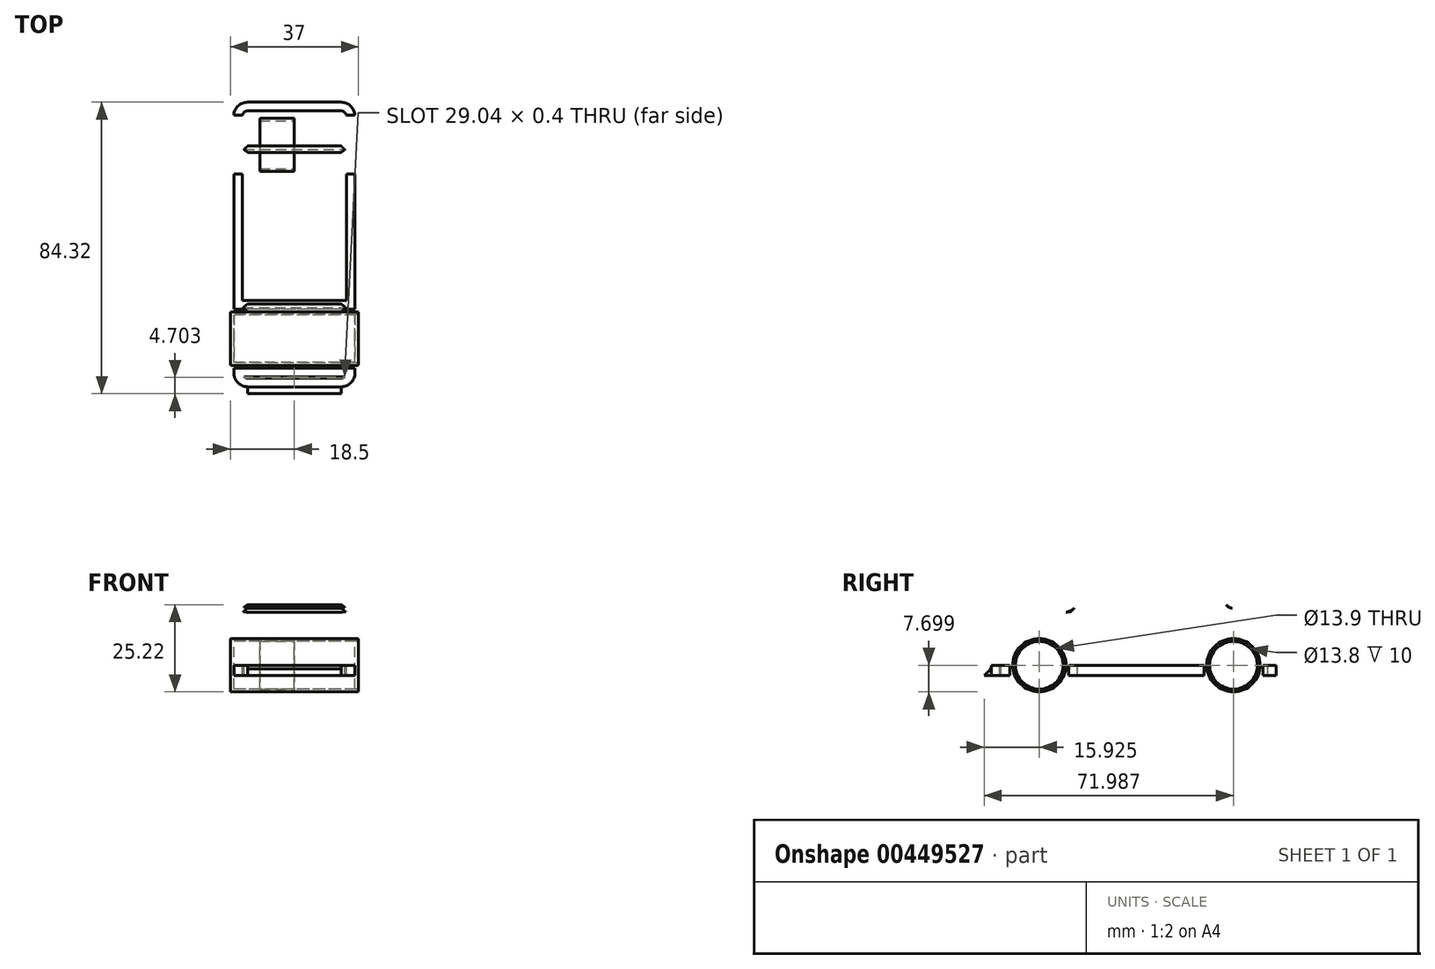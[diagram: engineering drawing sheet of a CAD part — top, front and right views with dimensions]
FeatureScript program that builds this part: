
annotation { "Feature Type Name" : "Feature", "Feature Type Description" : "" }
export const myFeature = defineFeature(function(context is Context, id is Id, definition is map)
    precondition{}
    {
        {
            var Q0;
            Q0=qCreatedBy(makeId("Right.planeOp"),FACE);
            var sketch = newSketch(context, id + "F0", { "sketchPlane" : qUnion([Q0])});
            skLineSegment(sketch, "E0", {"start": v(-46.86, -9.62) * mm, "end": v(35.46, -9.62) * mm});
            skLineSegment(sketch, "E1", {"start": v(35.46, -9.62) * mm, "end": v(35.46, 3.56) * mm});
            skLineSegment(sketch, "E2", {"start": v(35.46, 3.56) * mm, "end": v(21.74, 7.13) * mm});
            skLineSegment(sketch, "E3", {"start": v(21.74, 7.13) * mm, "end": v(13.72, 15.14) * mm});
            skLineSegment(sketch, "E4", {"start": v(13.72, 15.14) * mm, "end": v(-14.43, 15.14) * mm});
            skLineSegment(sketch, "E5", {"start": v(-14.43, 15.14) * mm, "end": v(-23.87, 5.88) * mm});
            skLineSegment(sketch, "E6", {"start": v(-23.87, 5.88) * mm, "end": v(-46.5, 3.03) * mm});
            skLineSegment(sketch, "E7", {"start": v(-46.5, 3.03) * mm, "end": v(-46.86, -9.62) * mm});
            skCircle(sketch, "E8", {"center": v(-32.94, -9.62) * mm, "radius": 8.52 * mm});
            skCircle(sketch, "E9", {"center": v(23.13, -9.62) * mm, "radius": 8.54 * mm});
            skSolve(sketch);
        }
        {
            var Q0;
            {var subQ4=sQuery(id+"F0.wireOp",EDGE,"E1");Q0=makeQuery(id+"F0.imprint","IMPRINT",FACE,{"disambiguationData":[TD([[makeQuery(id+"F0.imprint","IMPRINT",EDGE,{"derivedFrom":subQ4}),1.0]])]});}
            var Q1;
            {var subQ0=sQuery(id+"F0.wireOp",EDGE,"E8");var subQ1=sQuery(id+"F0.wireOp",EDGE,"E0");var subQ2=makeQuery(id+"F0.imprint","INTERSECT",VERTEX,{"disambiguationData":[OD(0.0)],"derivedFrom":[subQ1,subQ0]});Q1=makeQuery(id+"F0.imprint","IMPRINT",FACE,{"disambiguationData":[TD([[makeQuery(id+"F0.imprint","IMPRINT",EDGE,{"disambiguationData":[TD([[subQ2,-1.0]])],"derivedFrom":subQ1}),1.0]])]});}
            var Q2;
            {var subQ0=sQuery(id+"F0.wireOp",EDGE,"E9");var subQ1=sQuery(id+"F0.wireOp",EDGE,"E0");var subQ2=makeQuery(id+"F0.imprint","INTERSECT",VERTEX,{"disambiguationData":[OD(0.0)],"derivedFrom":[subQ1,subQ0]});Q2=makeQuery(id+"F0.imprint","IMPRINT",FACE,{"disambiguationData":[TD([[makeQuery(id+"F0.imprint","IMPRINT",EDGE,{"disambiguationData":[TD([[subQ2,-1.0]])],"derivedFrom":subQ1}),1.0]])]});}
            extrude(context, id + "F1", {"entities" : qUnion([Q0, Q1, Q2]), "endBound" : BoundingType.SYMMETRIC, "depth" : 35 * mm});
        }
        {
            var Q0;
            Q0=makeQuery(id+"F1.opExtrude","CAP_EDGE",EDGE,{"disambiguationData":[OSD([sQuery(id+"F0.wireOp",EDGE,"E7")])],"isStart":false});
            var Q1;
            Q1=makeQuery(id+"F1.opExtrude","CAP_EDGE",EDGE,{"disambiguationData":[OSD([sQuery(id+"F0.wireOp",EDGE,"E6")])],"isStart":false});
            var Q2;
            Q2=makeQuery(id+"F1.opExtrude","SWEPT_EDGE",EDGE,{"disambiguationData":[OSD([sQuery(id+"F0.wireOp",EDGE,"E6"),sQuery(id+"F0.wireOp",EDGE,"E7")])]});
            var Q3;
            Q3=makeQuery(id+"F1.opExtrude","CAP_EDGE",EDGE,{"disambiguationData":[OSD([sQuery(id+"F0.wireOp",EDGE,"E5")])],"isStart":false});
            var Q4;
            Q4=makeQuery(id+"F1.opExtrude","SWEPT_EDGE",EDGE,{"disambiguationData":[OSD([sQuery(id+"F0.wireOp",EDGE,"E4"),sQuery(id+"F0.wireOp",EDGE,"E5")])]});
            var Q5;
            Q5=makeQuery(id+"F1.opExtrude","SWEPT_EDGE",EDGE,{"disambiguationData":[OSD([sQuery(id+"F0.wireOp",EDGE,"E5"),sQuery(id+"F0.wireOp",EDGE,"E6")])]});
            var Q6;
            Q6=makeQuery(id+"F1.opExtrude","CAP_EDGE",EDGE,{"disambiguationData":[OSD([sQuery(id+"F0.wireOp",EDGE,"E4")])],"isStart":false});
            var Q7;
            Q7=makeQuery(id+"F1.opExtrude","SWEPT_EDGE",EDGE,{"disambiguationData":[OSD([sQuery(id+"F0.wireOp",EDGE,"E3"),sQuery(id+"F0.wireOp",EDGE,"E4")])]});
            var Q8;
            Q8=makeQuery(id+"F1.opExtrude","SWEPT_EDGE",EDGE,{"disambiguationData":[OSD([sQuery(id+"F0.wireOp",EDGE,"E2"),sQuery(id+"F0.wireOp",EDGE,"E3")])]});
            var Q9;
            Q9=makeQuery(id+"F1.opExtrude","CAP_EDGE",EDGE,{"disambiguationData":[OSD([sQuery(id+"F0.wireOp",EDGE,"E2")])],"isStart":false});
            var Q10;
            Q10=makeQuery(id+"F1.opExtrude","SWEPT_EDGE",EDGE,{"disambiguationData":[OSD([sQuery(id+"F0.wireOp",EDGE,"E1"),sQuery(id+"F0.wireOp",EDGE,"E2")])]});
            var Q11;
            Q11=makeQuery(id+"F1.opExtrude","CAP_EDGE",EDGE,{"disambiguationData":[OSD([sQuery(id+"F0.wireOp",EDGE,"E2")])],"isStart":true});
            var Q12;
            Q12=makeQuery(id+"F1.opExtrude","CAP_EDGE",EDGE,{"disambiguationData":[OSD([sQuery(id+"F0.wireOp",EDGE,"E1")])],"isStart":true});
            var Q13;
            Q13=makeQuery(id+"F1.opExtrude","CAP_EDGE",EDGE,{"disambiguationData":[OSD([sQuery(id+"F0.wireOp",EDGE,"E4")])],"isStart":true});
            var Q14;
            Q14=makeQuery(id+"F1.opExtrude","CAP_EDGE",EDGE,{"disambiguationData":[OSD([sQuery(id+"F0.wireOp",EDGE,"E5")])],"isStart":true});
            var Q15;
            Q15=makeQuery(id+"F1.opExtrude","CAP_EDGE",EDGE,{"disambiguationData":[OSD([sQuery(id+"F0.wireOp",EDGE,"E6")])],"isStart":true});
            var Q16;
            Q16=makeQuery(id+"F1.opExtrude","CAP_EDGE",EDGE,{"disambiguationData":[OSD([sQuery(id+"F0.wireOp",EDGE,"E7")])],"isStart":true});
            var Q17;
            Q17=makeQuery(id+"F1.opExtrude","CAP_EDGE",EDGE,{"disambiguationData":[OSD([sQuery(id+"F0.wireOp",EDGE,"E3")])],"isStart":false});
            var Q18;
            Q18=makeQuery(id+"F1.opExtrude","CAP_EDGE",EDGE,{"disambiguationData":[OSD([sQuery(id+"F0.wireOp",EDGE,"E3")])],"isStart":true});
            var Q19;
            Q19=makeQuery(id+"F1.opExtrude","CAP_EDGE",EDGE,{"disambiguationData":[OSD([sQuery(id+"F0.wireOp",EDGE,"E1")])],"isStart":false});
            fillet(context, id + "F2", {"entities" : qUnion([Q0, Q1, Q2, Q3, Q4, Q5, Q6, Q7, Q8, Q9, Q10, Q11, Q12, Q13, Q14, Q15, Q16, Q17, Q18, Q19]), "radius" : 4 * mm, "tangentPropagation" : true, "allowEdgeOverflow" : false});
        }
        {
            var Q0;
            Q0=makeQuery(id+"F1.opExtrude","SWEPT_FACE",FACE,{"disambiguationData":[OSD([sQuery(id+"F0.wireOp",EDGE,"E0")])]});
            shell(context, id + "F3", {"entities" : qUnion([Q0]), "thickness" : 2.5 * mm});
        }
        {
            var Q0;
            {var subQ0=sQuery(id+"F0.wireOp",EDGE,"E7");var subQ1=sQuery(id+"F0.wireOp",EDGE,"E6");var subQ2=sQuery(id+"F0.wireOp",EDGE,"E5");var subQ3=sQuery(id+"F0.wireOp",EDGE,"E4");var subQ4=sQuery(id+"F0.wireOp",EDGE,"E3");var subQ5=sQuery(id+"F0.wireOp",EDGE,"E2");var subQ6=sQuery(id+"F0.wireOp",EDGE,"E1");var subQ7=sQuery(id+"F0.wireOp",EDGE,"E0");var subQ8=makeQuery(id+"F1.opExtrude","CAP_FACE",FACE,{"disambiguationData":[OSD([subQ7,subQ6,subQ5,subQ4,subQ3,subQ2,subQ1,subQ0])],"isStart":true});Q0=makeQuery(id+"FvR2XKBQ7TzLp4t_1.boolean.opBoolean","SPLIT",FACE,{"disambiguationData":[TD([subQ8,makeQuery(id+"F3.opShell","OFFSET_FACE",FACE,{"disambiguationData":[OSD([subQ7,subQ6,subQ5,subQ4,subQ3,subQ2,subQ1,subQ0]),TDD([subQ8])]}),makeQuery(id+"FvR2XKBQ7TzLp4t_1.opExtrude","SWEPT_FACE",FACE,{"disambiguationData":[OSD([sQuery(id+"F0.wireOp",EDGE,"E8")])]}),makeQuery(id+"FvR2XKBQ7TzLp4t_1.opExtrude","SWEPT_FACE",FACE,{"disambiguationData":[OSD([sQuery(id+"F0.wireOp",EDGE,"E9")])]})])],"derivedFrom":makeQuery(id+"F1.opExtrude","SWEPT_FACE",FACE,{"disambiguationData":[OSD([subQ7])]})});}
            var Q1;
            {var subQ0=sQuery(id+"F0.wireOp",EDGE,"E7");var subQ1=makeQuery(id+"F1.opExtrude","SWEPT_FACE",FACE,{"disambiguationData":[OSD([subQ0])]});var subQ2=sQuery(id+"F0.wireOp",EDGE,"E6");var subQ3=sQuery(id+"F0.wireOp",EDGE,"E5");var subQ4=sQuery(id+"F0.wireOp",EDGE,"E4");var subQ5=sQuery(id+"F0.wireOp",EDGE,"E3");var subQ6=sQuery(id+"F0.wireOp",EDGE,"E2");var subQ7=sQuery(id+"F0.wireOp",EDGE,"E1");var subQ8=sQuery(id+"F0.wireOp",EDGE,"E0");var subQ9=makeQuery(id+"F1.opExtrude","CAP_FACE",FACE,{"disambiguationData":[OSD([subQ8,subQ7,subQ6,subQ5,subQ4,subQ3,subQ2,subQ0])],"isStart":false});var subQ10=makeQuery(id+"F1.opExtrude","CAP_FACE",FACE,{"disambiguationData":[OSD([subQ8,subQ7,subQ6,subQ5,subQ4,subQ3,subQ2,subQ0])],"isStart":true});var subQ11=makeQuery(id+"F2.opFillet","BLEND_FACE",FACE,{"disambiguationData":[OSD([subQ0]),TDD([makeQuery(id+"F1.opExtrude","CAP_EDGE",EDGE,{"disambiguationData":[OSD([subQ0])],"isStart":false})])]});var subQ12=makeQuery(id+"F2.opFillet","BLEND_FACE",FACE,{"disambiguationData":[OSD([subQ0]),TDD([makeQuery(id+"F1.opExtrude","CAP_EDGE",EDGE,{"disambiguationData":[OSD([subQ0])],"isStart":true})])]});Q1=makeQuery(id+"FvR2XKBQ7TzLp4t_1.boolean.opBoolean","SPLIT",FACE,{"disambiguationData":[TD([subQ10,subQ9,subQ1,subQ12,subQ11,makeQuery(id+"F3.opShell","OFFSET_FACE",FACE,{"disambiguationData":[OSD([subQ0]),TDD([subQ12])]}),makeQuery(id+"F3.opShell","OFFSET_FACE",FACE,{"disambiguationData":[OSD([subQ0]),TDD([subQ11])]}),makeQuery(id+"F3.opShell","OFFSET_FACE",FACE,{"disambiguationData":[OSD([subQ8,subQ7,subQ6,subQ5,subQ4,subQ3,subQ2,subQ0]),TDD([subQ10])]}),makeQuery(id+"F3.opShell","OFFSET_FACE",FACE,{"disambiguationData":[OSD([subQ8,subQ7,subQ6,subQ5,subQ4,subQ3,subQ2,subQ0]),TDD([subQ9])]}),makeQuery(id+"F3.opShell","OFFSET_FACE",FACE,{"disambiguationData":[OSD([subQ0]),TDD([subQ1])]}),makeQuery(id+"FvR2XKBQ7TzLp4t_1.opExtrude","SWEPT_FACE",FACE,{"disambiguationData":[OSD([sQuery(id+"F0.wireOp",EDGE,"E8")])]})])],"derivedFrom":makeQuery(id+"F1.opExtrude","SWEPT_FACE",FACE,{"disambiguationData":[OSD([subQ8])]})});}
            var Q2;
            {var subQ0=sQuery(id+"F0.wireOp",EDGE,"E7");var subQ1=sQuery(id+"F0.wireOp",EDGE,"E6");var subQ2=sQuery(id+"F0.wireOp",EDGE,"E5");var subQ3=sQuery(id+"F0.wireOp",EDGE,"E4");var subQ4=sQuery(id+"F0.wireOp",EDGE,"E3");var subQ5=sQuery(id+"F0.wireOp",EDGE,"E2");var subQ6=sQuery(id+"F0.wireOp",EDGE,"E1");var subQ7=sQuery(id+"F0.wireOp",EDGE,"E0");var subQ8=makeQuery(id+"F1.opExtrude","CAP_FACE",FACE,{"disambiguationData":[OSD([subQ7,subQ6,subQ5,subQ4,subQ3,subQ2,subQ1,subQ0])],"isStart":false});Q2=makeQuery(id+"FvR2XKBQ7TzLp4t_1.boolean.opBoolean","SPLIT",FACE,{"disambiguationData":[TD([subQ8,makeQuery(id+"F3.opShell","OFFSET_FACE",FACE,{"disambiguationData":[OSD([subQ7,subQ6,subQ5,subQ4,subQ3,subQ2,subQ1,subQ0]),TDD([subQ8])]}),makeQuery(id+"FvR2XKBQ7TzLp4t_1.opExtrude","SWEPT_FACE",FACE,{"disambiguationData":[OSD([sQuery(id+"F0.wireOp",EDGE,"E8")])]}),makeQuery(id+"FvR2XKBQ7TzLp4t_1.opExtrude","SWEPT_FACE",FACE,{"disambiguationData":[OSD([sQuery(id+"F0.wireOp",EDGE,"E9")])]})])],"derivedFrom":makeQuery(id+"F1.opExtrude","SWEPT_FACE",FACE,{"disambiguationData":[OSD([subQ7])]})});}
            var Q3;
            {var subQ0=sQuery(id+"F0.wireOp",EDGE,"E1");var subQ1=makeQuery(id+"F2.opFillet","BLEND_FACE",FACE,{"disambiguationData":[OSD([subQ0]),TDD([makeQuery(id+"F1.opExtrude","CAP_EDGE",EDGE,{"disambiguationData":[OSD([subQ0])],"isStart":true})])]});var subQ2=makeQuery(id+"F2.opFillet","BLEND_FACE",FACE,{"disambiguationData":[OSD([subQ0]),TDD([makeQuery(id+"F1.opExtrude","CAP_EDGE",EDGE,{"disambiguationData":[OSD([subQ0])],"isStart":false})])]});var subQ3=makeQuery(id+"F1.opExtrude","SWEPT_FACE",FACE,{"disambiguationData":[OSD([subQ0])]});Q3=makeQuery(id+"FvR2XKBQ7TzLp4t_1.boolean.opBoolean","SPLIT",FACE,{"disambiguationData":[TD([subQ3,subQ1,subQ2,makeQuery(id+"F3.opShell","OFFSET_FACE",FACE,{"disambiguationData":[OSD([subQ0]),TDD([subQ1])]}),makeQuery(id+"F3.opShell","OFFSET_FACE",FACE,{"disambiguationData":[OSD([subQ0]),TDD([subQ2])]}),makeQuery(id+"F3.opShell","OFFSET_FACE",FACE,{"disambiguationData":[OSD([subQ0]),TDD([subQ3])]}),makeQuery(id+"FvR2XKBQ7TzLp4t_1.opExtrude","SWEPT_FACE",FACE,{"disambiguationData":[OSD([sQuery(id+"F0.wireOp",EDGE,"E9")])]})])],"derivedFrom":makeQuery(id+"F1.opExtrude","SWEPT_FACE",FACE,{"disambiguationData":[OSD([sQuery(id+"F0.wireOp",EDGE,"E0")])]})});}
            extrude(context, id + "F4", {"entities" : qUnion([Q0, Q1, Q2, Q3]), "operationType" : NewBodyOperationType.ADD, "depth" : 3 * mm});
        }
        {
            var Q0;
            {var subQ0=sQuery(id+"F0.wireOp",EDGE,"E7");var subQ1=sQuery(id+"F0.wireOp",EDGE,"E0");Q0=makeQuery(id+"F4.opExtrude","SWEPT_FACE",FACE,{"disambiguationData":[OSD([subQ1,subQ0]),TDD([makeQuery(id+"F1.opExtrude","SWEPT_EDGE",EDGE,{"disambiguationData":[OSD([subQ1,subQ0])]})])]});}
            extrude(context, id + "F5", {"entities" : qUnion([Q0]), "operationType" : NewBodyOperationType.ADD, "depth" : 2 * mm});
        }
        {
            var Q0;
            {var subQ0=sQuery(id+"F0.wireOp",EDGE,"E7");var subQ1=sQuery(id+"F0.wireOp",EDGE,"E0");var subQ2=makeQuery(id+"F1.opExtrude","SWEPT_EDGE",EDGE,{"disambiguationData":[OSD([subQ1,subQ0])]});Q0=makeQuery(id+"F5.opExtrude","CAP_EDGE",EDGE,{"disambiguationData":[OSD([subQ1,subQ0]),TDD([makeQuery(id+"F4.boolean.opBoolean","MERGE",EDGE,{"derivedFrom":[subQ2,makeQuery(id+"F4.opExtrude","CAP_EDGE",EDGE,{"disambiguationData":[OSD([subQ1,subQ0]),TDD([subQ2])],"isStart":true})]})])],"isStart":false});}
            chamfer(context, id + "F6", {"entities" : qUnion([Q0]), "width" : 3 * mm, "tangentPropagation" : true});
        }
        {
            var Q0;
            Q0=makeQuery(id+"F1.opExtrude","SWEPT_FACE",FACE,{"disambiguationData":[OSD([sQuery(id+"F0.wireOp",EDGE,"E5")])]});
            extrude(context, id + "F7", {"entities" : qUnion([Q0]), "operationType" : NewBodyOperationType.REMOVE, "oppositeDirection" : true, "depth" : 2.5 * mm});
        }
        {
            var Q0;
            {var subQ0=sQuery(id+"F0.wireOp",EDGE,"E5");var subQ1=makeQuery(id+"F2.opFillet","BLEND_EDGE",EDGE,{"blendedFrom":[makeQuery(id+"F1.opExtrude","CAP_EDGE",EDGE,{"disambiguationData":[OSD([subQ0])],"isStart":true}),makeQuery(id+"F1.opExtrude","SWEPT_FACE",FACE,{"disambiguationData":[OSD([subQ0])]})],"blendedInto":[makeQuery(id+"F1.opExtrude","SWEPT_FACE",FACE,{"disambiguationData":[OSD([subQ0])]})]});Q0=makeQuery(id+"F7.boolean.opBoolean","MERGE",EDGE,{"derivedFrom":[makeQuery(id+"F3.opShell","OFFSET_EDGE",EDGE,{"disambiguationData":[OSD([subQ0]),TDD([subQ1])]}),makeQuery(id+"F7.opExtrude","CAP_EDGE",EDGE,{"disambiguationData":[OSD([subQ0]),TDD([subQ1])],"isStart":false})]});}
            chamfer(context, id + "F8", {"entities" : qUnion([Q0]), "width" : 5 * mm, "tangentPropagation" : true});
        }
        {
            var Q0;
            Q0=qCreatedBy(makeId("Right.planeOp"),FACE);
            var sketch = newSketch(context, id + "F9", { "sketchPlane" : qUnion([Q0])});
            skLineSegment(sketch, "E10", {"start": v(-12.8, 11.13) * mm, "end": v(-21.96, 2.12) * mm});
            skLineSegment(sketch, "E11", {"start": v(-21.96, 2.12) * mm, "end": v(-1.75, 2.12) * mm});
            skLineSegment(sketch, "E12", {"start": v(-1.75, 2.12) * mm, "end": v(-1.75, 11.1) * mm});
            skLineSegment(sketch, "E13", {"start": v(-1.75, 11.1) * mm, "end": v(-12.8, 11.13) * mm});
            skLineSegment(sketch, "E14", {"start": v(1.62, 2.12) * mm, "end": v(1.62, 11.03) * mm});
            skLineSegment(sketch, "E15", {"start": v(1.62, 11.03) * mm, "end": v(12.11, 11.03) * mm});
            skLineSegment(sketch, "E16", {"start": v(12.11, 11.03) * mm, "end": v(20.89, 2.12) * mm});
            skLineSegment(sketch, "E17", {"start": v(20.89, 2.12) * mm, "end": v(1.62, 2.12) * mm});
            skSolve(sketch);
        }
        {
            var Q0;
            Q0 = qSketchRegion(id + "F9", true);
            extrude(context, id + "F10", {"entities" : qUnion([Q0]), "operationType" : NewBodyOperationType.REMOVE, "endBound" : BoundingType.SYMMETRIC, "oppositeDirection" : true, "depth" : 35 * mm});
        }
        {
            var Q0;
            {var subQ0=sQuery(id+"F0.wireOp",EDGE,"E8");var subQ1=sQuery(id+"F0.wireOp",EDGE,"E0");var subQ2=makeQuery(id+"F0.imprint","INTERSECT",VERTEX,{"disambiguationData":[OD(0.0)],"derivedFrom":[subQ1,subQ0]});Q0=makeQuery(id+"F0.imprint","IMPRINT",FACE,{"disambiguationData":[TD([[makeQuery(id+"F0.imprint","IMPRINT",EDGE,{"disambiguationData":[TD([[subQ2,-1.0]])],"derivedFrom":subQ1}),1.0]])]});}
            var Q1;
            {var subQ0=sQuery(id+"F0.wireOp",EDGE,"E9");var subQ1=sQuery(id+"F0.wireOp",EDGE,"E0");var subQ2=makeQuery(id+"F0.imprint","INTERSECT",VERTEX,{"disambiguationData":[OD(0.0)],"derivedFrom":[subQ1,subQ0]});Q1=makeQuery(id+"F0.imprint","IMPRINT",FACE,{"disambiguationData":[TD([[makeQuery(id+"F0.imprint","IMPRINT",EDGE,{"disambiguationData":[TD([[subQ2,-1.0]])],"derivedFrom":subQ1}),1.0]])]});}
            extrude(context, id + "F11", {"entities" : qUnion([Q0, Q1]), "operationType" : NewBodyOperationType.REMOVE, "endBound" : BoundingType.SYMMETRIC, "oppositeDirection" : true, "depth" : 35 * mm});
        }
        {
            var Q0;
            Q0=qCreatedBy(makeId("Right.planeOp"),FACE);
            var sketch = newSketch(context, id + "F12", { "sketchPlane" : qUnion([Q0])});
            skLineSegment(sketch, "E18", {"start": v(-41.46, -9.6) * mm, "end": v(-41.46, -13.06) * mm});
            skLineSegment(sketch, "E19", {"start": v(-24.44, -9.5) * mm, "end": v(-24.44, -13.08) * mm});
            skLineSegment(sketch, "E20", {"start": v(-24.44, -13.08) * mm, "end": v(-41.46, -13.06) * mm});
            skLineSegment(sketch, "E21", {"start": v(-41.46, -9.6) * mm, "end": v(-24.44, -9.5) * mm});
            skSolve(sketch);
        }
        {
            var Q0;
            Q0 = qSketchRegion(id + "F12", true);
            extrude(context, id + "F13", {"entities" : qUnion([Q0]), "operationType" : NewBodyOperationType.REMOVE, "endBound" : BoundingType.SYMMETRIC, "oppositeDirection" : true, "depth" : 35 * mm});
        }
        {
            var Q0;
            Q0=qCreatedBy(makeId("Right.planeOp"),FACE);
            var sketch = newSketch(context, id + "F14", { "sketchPlane" : qUnion([Q0])});
            skLineSegment(sketch, "E22", {"start": v(14.62, -9.53) * mm, "end": v(14.62, -13.62) * mm});
            skLineSegment(sketch, "E23", {"start": v(31.64, -9.47) * mm, "end": v(31.64, -13.06) * mm});
            skLineSegment(sketch, "E24", {"start": v(31.64, -13.06) * mm, "end": v(14.62, -13.62) * mm});
            skLineSegment(sketch, "E25", {"start": v(14.62, -9.53) * mm, "end": v(31.64, -9.47) * mm});
            skSolve(sketch);
        }
        {
            var Q0;
            Q0 = qSketchRegion(id + "F14", true);
            extrude(context, id + "F15", {"entities" : qUnion([Q0]), "operationType" : NewBodyOperationType.REMOVE, "endBound" : BoundingType.SYMMETRIC, "oppositeDirection" : true, "depth" : 35 * mm});
        }
        {
            var Q0;
            Q0 = qSketchRegion(id + "F9", true);
            extrude(context, id + "F16", {"entities" : qUnion([Q0]), "operationType" : NewBodyOperationType.REMOVE, "oppositeDirection" : true, "depth" : 35 * mm});
        }
        {
            var Q0;
            {var subQ0=sQuery(id+"F0.wireOp",EDGE,"E8");var subQ1=sQuery(id+"F0.wireOp",EDGE,"E0");var subQ2=makeQuery(id+"F0.imprint","INTERSECT",VERTEX,{"disambiguationData":[OD(0.0)],"derivedFrom":[subQ1,subQ0]});Q0=makeQuery(id+"F0.imprint","IMPRINT",FACE,{"disambiguationData":[TD([[makeQuery(id+"F0.imprint","IMPRINT",EDGE,{"disambiguationData":[TD([[subQ2,-1.0]])],"derivedFrom":subQ1}),1.0]])]});}
            var sketch = newSketch(context, id + "F17", { "sketchPlane" : qUnion([Q0])});
            skCircle(sketch, "E26", {"center": v(-32.94, -9.62) * mm, "radius": 7.7 * mm});
            skCircle(sketch, "E27", {"center": v(-32.94, -9.62) * mm, "radius": 6.9 * mm});
            skCircle(sketch, "E28", {"center": v(23.13, -9.62) * mm, "radius": 7.7 * mm});
            skCircle(sketch, "E29", {"center": v(23.13, -9.62) * mm, "radius": 6.9 * mm});
            skCircle(sketch, "E30", {"center": v(-32.94, -9.62) * mm, "radius": 6.95 * mm});
            skSolve(sketch);
        }
        {
            var Q0;
            {var subQ0=sQuery(id+"F17.wireOp",EDGE,"E26");var subQ1=sQuery(id+"F0.wireOp",EDGE,"E8");var subQ2=sQuery(id+"F0.wireOp",EDGE,"E0");var subQ3=makeQuery(id+"F0.imprint","IMPRINT",EDGE,{"disambiguationData":[TD([[makeQuery(id+"F0.imprint","INTERSECT",VERTEX,{"disambiguationData":[OD(0.0)],"derivedFrom":[subQ2,subQ1]}),-1.0]])],"derivedFrom":subQ2});var subQ4=makeQuery(id+"F17.imprint","INTERSECT",VERTEX,{"disambiguationData":[OD(0.0)],"derivedFrom":[subQ3,subQ0]});Q0=makeQuery(id+"F17.imprint","IMPRINT",FACE,{"disambiguationData":[TD([[makeQuery(id+"F17.imprint","IMPRINT",EDGE,{"disambiguationData":[TD([[subQ4,-1.0]])],"derivedFrom":subQ0}),1.0]])]});}
            var Q1;
            {var subQ0=sQuery(id+"F17.wireOp",EDGE,"E26");var subQ1=sQuery(id+"F0.wireOp",EDGE,"E8");var subQ2=sQuery(id+"F0.wireOp",EDGE,"E0");var subQ3=makeQuery(id+"F0.imprint","IMPRINT",EDGE,{"disambiguationData":[TD([[makeQuery(id+"F0.imprint","INTERSECT",VERTEX,{"disambiguationData":[OD(0.0)],"derivedFrom":[subQ2,subQ1]}),-1.0]])],"derivedFrom":subQ2});var subQ4=makeQuery(id+"F17.imprint","INTERSECT",VERTEX,{"disambiguationData":[OD(0.0)],"derivedFrom":[subQ3,subQ0]});Q1=makeQuery(id+"F17.imprint","IMPRINT",FACE,{"disambiguationData":[TD([[makeQuery(id+"F17.imprint","IMPRINT",EDGE,{"disambiguationData":[TD([[subQ4,1.0]])],"derivedFrom":subQ0}),1.0]])]});}
            var Q2;
            Q2=sQuery(id+"F17.wireOp",EDGE,"E26");
            var Q3;
            Q3=sQuery(id+"F17.wireOp",EDGE,"E27");
            extrude(context, id + "F18", {"entities" : qUnion([Q0, Q1]), "surfaceEntities" : qUnion([Q2, Q3]), "endBound" : BoundingType.SYMMETRIC, "depth" : 37 * mm});
        }
        {
            var Q0;
            {var subQ0=sQuery(id+"F17.wireOp",EDGE,"E27");var subQ1=sQuery(id+"F0.wireOp",EDGE,"E8");var subQ2=sQuery(id+"F0.wireOp",EDGE,"E0");var subQ3=makeQuery(id+"F0.imprint","IMPRINT",EDGE,{"disambiguationData":[TD([[makeQuery(id+"F0.imprint","INTERSECT",VERTEX,{"disambiguationData":[OD(0.0)],"derivedFrom":[subQ2,subQ1]}),-1.0]])],"derivedFrom":subQ2});var subQ4=makeQuery(id+"F17.imprint","INTERSECT",VERTEX,{"disambiguationData":[OD(0.0)],"derivedFrom":[subQ3,subQ0]});Q0=makeQuery(id+"F17.imprint","IMPRINT",FACE,{"disambiguationData":[TD([[makeQuery(id+"F17.imprint","IMPRINT",EDGE,{"disambiguationData":[TD([[subQ4,-1.0]])],"derivedFrom":subQ0}),1.0]])]});}
            var Q1;
            {var subQ0=sQuery(id+"F17.wireOp",EDGE,"E27");var subQ1=sQuery(id+"F0.wireOp",EDGE,"E8");var subQ2=sQuery(id+"F0.wireOp",EDGE,"E0");var subQ3=makeQuery(id+"F0.imprint","IMPRINT",EDGE,{"disambiguationData":[TD([[makeQuery(id+"F0.imprint","INTERSECT",VERTEX,{"disambiguationData":[OD(0.0)],"derivedFrom":[subQ2,subQ1]}),-1.0]])],"derivedFrom":subQ2});var subQ4=makeQuery(id+"F17.imprint","INTERSECT",VERTEX,{"disambiguationData":[OD(0.0)],"derivedFrom":[subQ3,subQ0]});Q1=makeQuery(id+"F17.imprint","IMPRINT",FACE,{"disambiguationData":[TD([[makeQuery(id+"F17.imprint","IMPRINT",EDGE,{"disambiguationData":[TD([[subQ4,1.0]])],"derivedFrom":subQ0}),1.0]])]});}
            extrude(context, id + "F19", {"entities" : qUnion([Q0, Q1]), "endBound" : BoundingType.SYMMETRIC, "depth" : 35 * mm});
        }
        {
            var Q0;
            Q0=makeQuery(id+"F18.opExtrude","CAP_EDGE",EDGE,{"disambiguationData":[OSD([sQuery(id+"F17.wireOp",EDGE,"E30")])],"isStart":false});
            var Q1;
            Q1=makeQuery(id+"F18.opExtrude","CAP_EDGE",EDGE,{"disambiguationData":[OSD([sQuery(id+"F17.wireOp",EDGE,"E26")])],"isStart":false});
            fillet(context, id + "F20", {"entities" : qUnion([Q0, Q1]), "radius" : 0.3 * mm, "tangentPropagation" : true, "allowEdgeOverflow" : false});
        }
        {
            var Q0;
            Q0=makeQuery(id+"F18.opExtrude","CAP_EDGE",EDGE,{"disambiguationData":[OSD([sQuery(id+"F17.wireOp",EDGE,"E26")])],"isStart":true});
            var Q1;
            Q1=makeQuery(id+"F18.opExtrude","CAP_EDGE",EDGE,{"disambiguationData":[OSD([sQuery(id+"F17.wireOp",EDGE,"E30")])],"isStart":true});
            fillet(context, id + "F21", {"entities" : qUnion([Q0, Q1]), "radius" : 0.3 * mm, "tangentPropagation" : true, "allowEdgeOverflow" : false});
        }
        {
            var Q0;
            Q0 = qSketchRegion(id + "F17", true);
            extrude(context, id + "F22", {"entities" : qUnion([Q0]), "operationType" : NewBodyOperationType.ADD, "depth" : -10 * mm, "offsetDistance" : 25 * mm});
        }
    });
